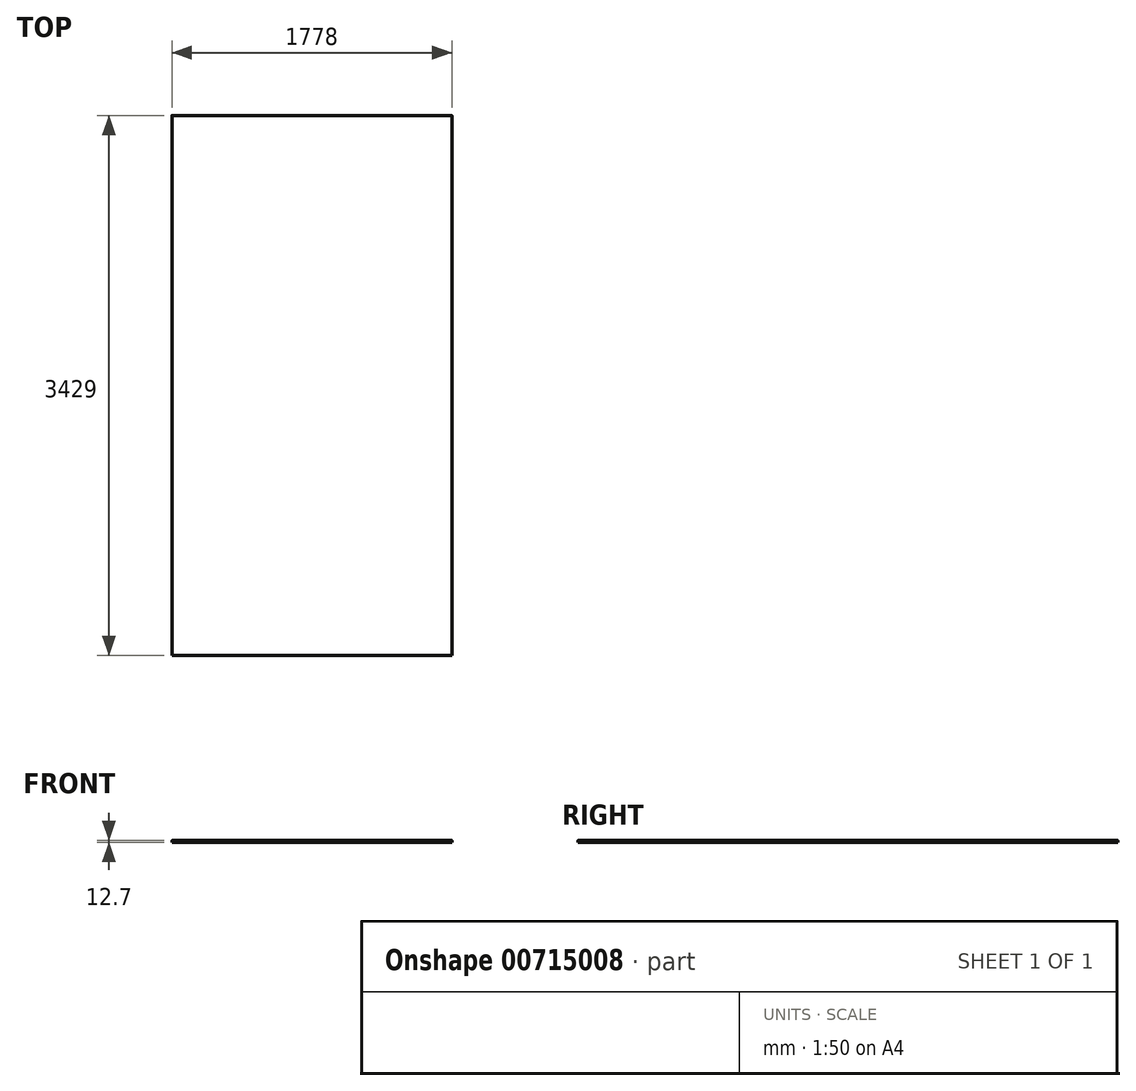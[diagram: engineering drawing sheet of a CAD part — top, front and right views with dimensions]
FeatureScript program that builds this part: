
annotation { "Feature Type Name" : "Feature", "Feature Type Description" : "" }
export const myFeature = defineFeature(function(context is Context, id is Id, definition is map)
    precondition{}
    {
        {
            var Q0;
            Q0=qCreatedBy(makeId("Top.planeOp"),FACE);
            var sketch = newSketch(context, id + "F0", { "sketchPlane" : qUnion([Q0])});
            skLineSegment(sketch, "E0.bottom", {"start": v(1617.02, -29.09) * mm, "end": v(-160.98, -29.09) * mm});
            skLineSegment(sketch, "E0.top", {"start": v(1617.02, 3399.91) * mm, "end": v(-160.98, 3399.91) * mm});
            skLineSegment(sketch, "E0.left", {"start": v(1617.02, -29.09) * mm, "end": v(1617.02, 3399.91) * mm});
            skLineSegment(sketch, "E0.right", {"start": v(-160.98, -29.09) * mm, "end": v(-160.98, 3399.91) * mm});
            skPoint(sketch, "E0.middle", {"position": v(728.02, 1685.41) * mm});
            skSolve(sketch);
        }
        {
            var Q0;
            Q0=makeQuery(id+"F0.imprint","IMPRINT",FACE,{"disambiguationData":[TD([[makeQuery(id+"F0.imprint","IMPRINT",EDGE,{"derivedFrom":sQuery(id+"F0.wireOp",EDGE,"E0.bottom")}),-1.0]])]});
            extrude(context, id + "F1", {"entities" : qUnion([Q0]), "depth" : 12.7 * mm, "offsetDistance" : 25.4 * mm});
        }
        {
            var Q0;
            Q0=makeQuery(id+"F1.opExtrude","CAP_EDGE",EDGE,{"disambiguationData":[OSD([sQuery(id+"F0.wireOp",EDGE,"E0.right")])],"isStart":false});
            var Q1;
            Q1=makeQuery(id+"F1.opExtrude","CAP_EDGE",EDGE,{"disambiguationData":[OSD([sQuery(id+"F0.wireOp",EDGE,"E0.bottom")])],"isStart":false});
            var Q2;
            Q2=makeQuery(id+"F1.opExtrude","CAP_EDGE",EDGE,{"disambiguationData":[OSD([sQuery(id+"F0.wireOp",EDGE,"E0.top")])],"isStart":false});
            var Q3;
            Q3=makeQuery(id+"F1.opExtrude","CAP_EDGE",EDGE,{"disambiguationData":[OSD([sQuery(id+"F0.wireOp",EDGE,"E0.left")])],"isStart":false});
            fillet(context, id + "F2", {"entities" : qUnion([Q0, Q1, Q2, Q3]), "radius" : 2.54 * mm, "tangentPropagation" : true, "allowEdgeOverflow" : false});
        }
    });
